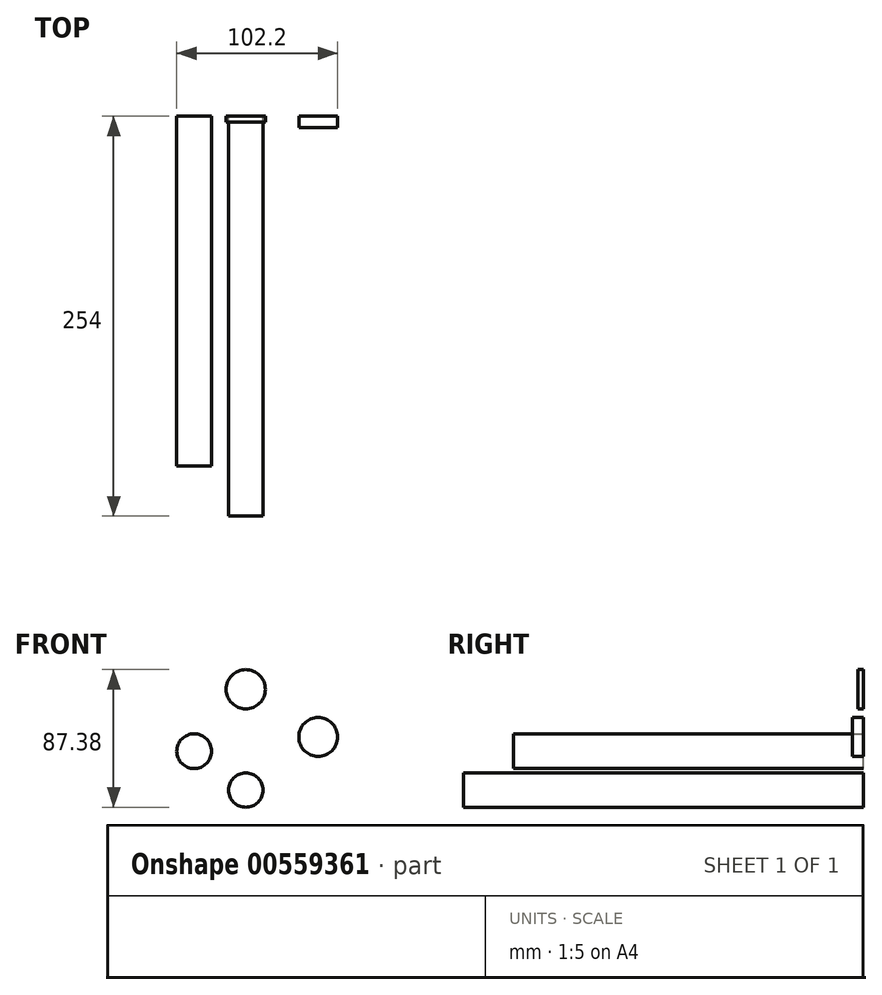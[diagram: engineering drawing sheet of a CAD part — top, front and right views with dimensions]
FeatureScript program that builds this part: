
annotation { "Feature Type Name" : "Feature", "Feature Type Description" : "" }
export const myFeature = defineFeature(function(context is Context, id is Id, definition is map)
    precondition{}
    {
        {
            var Q0;
            Q0=qCreatedBy(makeId("Front.planeOp"),FACE);
            var sketch = newSketch(context, id + "F0", { "sketchPlane" : qUnion([Q0])});
            skCircle(sketch, "E0", {"center": v(0, 0) * mm, "radius": 10.9 * mm});
            skSolve(sketch);
        }
        {
            var Q0;
            Q0=makeQuery(id+"F0.imprint","IMPRINT",FACE,{"disambiguationData":[TD([[makeQuery(id+"F0.imprint","IMPRINT",EDGE,{"derivedFrom":sQuery(id+"F0.wireOp",EDGE,"E0")}),1.0]])]});
            extrude(context, id + "F1", {"entities" : qUnion([Q0]), "depth" : 254 * mm, "offsetDistance" : 25.4 * mm});
        }
        {
            var Q0;
            Q0=qCreatedBy(makeId("Front.planeOp"),FACE);
            var sketch = newSketch(context, id + "F2", { "sketchPlane" : qUnion([Q0])});
            skCircle(sketch, "E1", {"center": v(-32.82, 24.7) * mm, "radius": 11.05 * mm});
            skSolve(sketch);
        }
        {
            var Q0;
            Q0=makeQuery(id+"F2.imprint","IMPRINT",FACE,{"disambiguationData":[TD([[makeQuery(id+"F2.imprint","IMPRINT",EDGE,{"derivedFrom":sQuery(id+"F2.wireOp",EDGE,"E1")}),1.0]])]});
            extrude(context, id + "F3", {"entities" : qUnion([Q0]), "depth" : 222.25 * mm, "offsetDistance" : 25.4 * mm});
        }
        {
            var Q0;
            Q0=qCreatedBy(makeId("Front.planeOp"),FACE);
            var sketch = newSketch(context, id + "F4", { "sketchPlane" : qUnion([Q0])});
            skCircle(sketch, "E2", {"center": v(46.01, 33.74) * mm, "radius": 12.32 * mm});
            skSolve(sketch);
        }
        {
            var Q0;
            Q0=makeQuery(id+"F4.imprint","IMPRINT",FACE,{"disambiguationData":[TD([[makeQuery(id+"F4.imprint","IMPRINT",EDGE,{"derivedFrom":sQuery(id+"F4.wireOp",EDGE,"E2")}),1.0]])]});
            extrude(context, id + "F5", {"entities" : qUnion([Q0]), "depth" : 7.11 * mm, "offsetDistance" : 25.4 * mm});
        }
        {
            var Q0;
            Q0=qCreatedBy(makeId("Front.planeOp"),FACE);
            var sketch = newSketch(context, id + "F6", { "sketchPlane" : qUnion([Q0])});
            skCircle(sketch, "E3", {"center": v(0, 64.04) * mm, "radius": 12.45 * mm});
            skSolve(sketch);
        }
        {
            var Q0;
            Q0=makeQuery(id+"F6.imprint","IMPRINT",FACE,{"disambiguationData":[TD([[makeQuery(id+"F6.imprint","IMPRINT",EDGE,{"derivedFrom":sQuery(id+"F6.wireOp",EDGE,"E3")}),1.0]])]});
            extrude(context, id + "F7", {"entities" : qUnion([Q0]), "depth" : 3.56 * mm, "offsetDistance" : 25.4 * mm});
        }
    });
